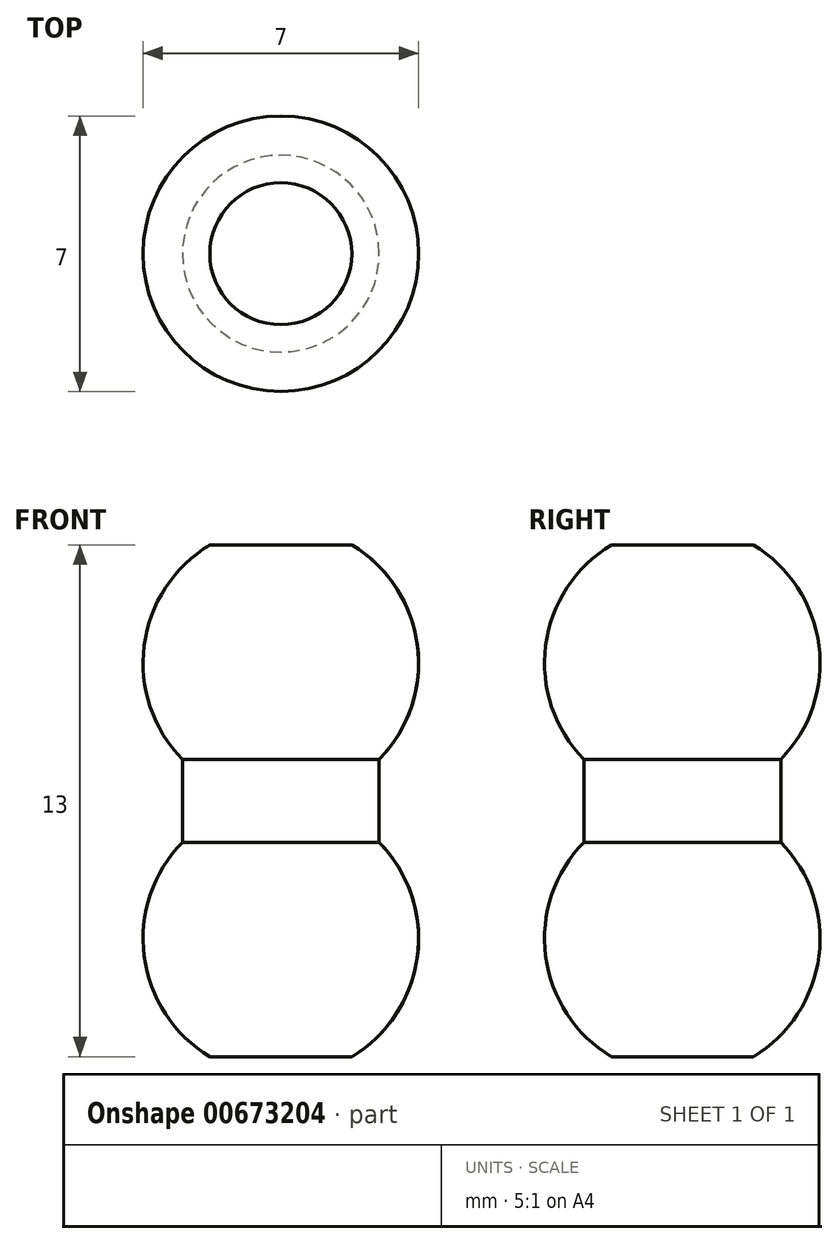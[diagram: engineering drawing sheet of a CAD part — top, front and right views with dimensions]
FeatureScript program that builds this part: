
annotation { "Feature Type Name" : "Feature", "Feature Type Description" : "" }
export const myFeature = defineFeature(function(context is Context, id is Id, definition is map)
    precondition{}
    {
        {
            var Q0;
            Q0=qCreatedBy(makeId("Right.planeOp"),FACE);
            var sketch = newSketch(context, id + "F0", { "sketchPlane" : qUnion([Q0])});
            skLineSegment(sketch, "E0", {"start": v(0, 0) * mm, "end": v(0, -7) * mm});
            skArc(sketch, "E1", {"start": v(-2.5, -4.55) * mm, "mid": v(-3.47, -7.44) * mm, "end": v(-1.8, -10) * mm});
            skArc(sketch, "E2", {"start": v(-1.8, 3) * mm, "mid": v(-3.47, 0.44) * mm, "end": v(-2.5, -2.45) * mm});
            skLineSegment(sketch, "E3", {"start": v(0, 0) * mm, "end": v(-2.5, 0) * mm, "construction": true});
            skLineSegment(sketch, "E4", {"start": v(-2.5, -2.45) * mm, "end": v(-2.5, -4.55) * mm});
            skLineSegment(sketch, "E5", {"start": v(0, 3) * mm, "end": v(0, -10) * mm});
            skLineSegment(sketch, "E6", {"start": v(0, 3) * mm, "end": v(-1.8, 3) * mm});
            skPoint(sketch, "E7.start.orphan", {"position": v(0.79, 3.5) * mm});
            skPoint(sketch, "E8.orphan", {"position": v(0, 3.5) * mm});
            skLineSegment(sketch, "E9", {"start": v(0, -10) * mm, "end": v(-1.8, -10) * mm});
            skPoint(sketch, "E10.start.orphan", {"position": v(0.54, -10.5) * mm});
            skPoint(sketch, "E11.orphan", {"position": v(0, -10.5) * mm});
            skSolve(sketch);
        }
        {
            var Q0;
            Q0=qSketchRegion(id+"F0",true);
            var Q1;
            Q1=sQuery(id+"F0.wireOp",EDGE,"E5");
            revolve(context, id + "F1", {"entities" : qUnion([Q0]), "axis" : qUnion([Q1]), "revolveType" : RevolveType.FULL});
        }
    });
